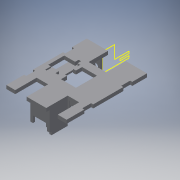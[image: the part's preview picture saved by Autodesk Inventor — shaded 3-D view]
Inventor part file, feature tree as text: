
AUTODESK INVENTOR PART (.ipt)
format: ipt  version: 2016 (Build 200138000, 138)  size: 613,376 bytes
history: native  units: in
note: dims shown in document units (in); Inventor stores cm internally (conversion verified against a paired STEP export)
features: reference x41, extrude x30, sketch x30, plane x6, projected_geometry x3
ambient origin geometry x8: Origin, YZ Plane, XZ Plane, XY Plane, X Axis, Y Axis, Z Axis, Center Point
bodies: Solid1 (feature_tree)
feature tree (110):
  extrude  "Extrusion1"  Depth=3.0in
  extrude  "Extrusion2"  Depth=0.0787in
  extrude  "Extrusion3"  Depth=1.0827in
  extrude  "Extrusion5"  Depth=1.0in TaperAngle=0.0deg
  plane  "Work Plane1"
  extrude  "Extrusion6"  Depth=0.0098in
  extrude  "Extrusion9"  Depth=0.0787in
  extrude  "Extrusion14"  Depth=0.1575in
  extrude  "Extrusion15"  Depth=1.25in
  plane  "Work Plane2"
  extrude  "Extrusion16"  Depth=0.1575in
  extrude  "Extrusion17"  Depth=0.9201in TaperAngle=0.0deg
  extrude  "Extrusion18"  Depth=0.1969in
  plane  "Work Plane3"
  extrude  "Extrusion20"  Depth=0.1969in TaperAngle=0.0deg
  extrude  "Extrusion21"  Depth=0.1181in TaperAngle=0.0deg
  plane  "Work Plane4"
  plane  "Work Plane5"
  extrude  "Extrusion23"  Depth=0.1181in
  extrude  "Extrusion24"  Depth=0.1969in TaperAngle=0.0deg
  plane  "Work Plane6"
  extrude  "Extrusion25"  Depth=0.35in
  extrude  "Extrusion26"  Depth=0.2in
  extrude  "Extrusion27"  Depth=0.1969in TaperAngle=0.0deg
  extrude  "Extrusion28"  Depth=1.5in
  extrude  "Extrusion29"  Depth=0.1181in
  extrude  "Extrusion30"  Depth=0.1181in TaperAngle=0.0deg
  extrude  "Extrusion31"  Depth=1.0in
  extrude  "Extrusion34"  Depth=0.5in
  sketch  "Sketch36"  dims[d105=0.1181in d106=0.5in]
  extrude  "Extrusion35"  Depth=0.5in
  extrude  "Extrusion36"  Depth=0.0197in
  extrude  "Extrusion37"  Depth=0.325in
  extrude  "Extrusion38"  Depth=0.1969in
  extrude  "Extrusion39"  Depth=0.1181in
  sketch  "Sketch41"  dims[d117=0.1969in d118=0.1181in]
  extrude  "Extrusion40"  Depth=0.1575in TaperAngle=0.0deg
  extrude  "Extrusion41"  Depth=1.0in TaperAngle=0.0deg
  sketch  "Sketch1"  dims[d0=4.5in d1=3.0in]
  sketch  "Sketch2"  dims[d2=0.1969in d3=0.0in d5=0.0787in]
  reference  "Reference1"
  reference  "Reference2"
  sketch  "Sketch3"  dims[d6=1.0in d7=0.0in d8=1.0827in]
  sketch  "Sketch5"  dims[d9=0.3937in d10=1.0in d11=0.0in]
  reference  "Reference14"
  reference  "Reference15"
  reference  "Reference16"
  reference  "Reference17"
  reference  "Reference18"
  sketch  "Sketch6"  dims[d12=0.0787in d23=0.0098in]
  reference  "Reference19"
  sketch  "Sketch9"  dims[d24=0.1575in d25=0.0787in]
  projected_geometry  "Projected Loop2"
  sketch  "Sketch14"  dims[d26=0.0098in d27=0.1575in]
  sketch  "Sketch15"  dims[d28=0.1181in d29=0.0in d30=1.25in]
  sketch  "Sketch16"  dims[d31=0.1575in d32=0.1575in]
  reference  "Reference30"
  sketch  "Sketch17"  dims[d33=0.1181in d34=0.0in d46=0.9201in d47=0.0in]
  reference  "Reference31"
  reference  "Reference32"
  reference  "Reference33"
  reference  "Reference35"
  reference  "Reference36"
  reference  "Reference37"
  reference  "Reference38"
  reference  "Reference39"
  reference  "Reference40"
  reference  "Reference41"
  reference  "Reference42"
  reference  "Reference43"
  reference  "Reference44"
  reference  "Reference45"
  reference  "Reference46"
  reference  "Reference47"
  reference  "Reference48"
  reference  "Reference49"
  sketch  "Sketch20"  dims[d58=0.1969in d59=0.1969in]
  reference  "Reference50"
  sketch  "Sketch21"  dims[d60=0.1969in d61=0.1969in d62=0.0in]
  sketch  "Sketch23"  dims[d63=1.0in d64=0.0in d65=0.1181in d66=0.0in]
  reference  "Reference53"
  reference  "Reference54"
  sketch  "Sketch24"  dims[d67=0.1969in d68=0.0in d69=0.1181in]
  sketch  "Sketch25"  dims[d70=0.1181in d71=0.1969in d72=0.0in]
  reference  "Reference55"
  reference  "Reference56"
  sketch  "Sketch26"  dims[d75=0.0394in d76=0.35in]
  reference  "Reference57"
  reference  "Reference58"
  sketch  "Sketch28"  dims[d77=0.1628in d78=0.2in]
  sketch  "Sketch29"  dims[d79=0.0787in d80=0.0in d81=0.1969in d82=0.0in]
  sketch  "Sketch30"  dims[d89=1.5in d90=1.5in]
  reference  "Reference59"
  sketch  "Sketch31"  dims[d91=0.1181in d92=0.0in d93=0.7in]
  sketch  "Sketch32"  dims[d94=1.26in d95=0.0in d96=0.1181in d97=0.0in]
  sketch  "Sketch35"  dims[d98=0.1181in d99=0.0in d104=1.0in]
  reference  "Reference61"
  sketch  "Sketch37"  dims[d107=1.0in d108=0.5in]
  reference  "Reference62"
  sketch  "Sketch38"  dims[d109=10.0in d110=0.0in d111=0.0197in]
  reference  "Reference63"
  sketch  "Sketch39"  dims[d112=0.0197in d113=0.325in]
  reference  "Reference64"
  sketch  "Sketch40"  dims[d114=0.197in d115=0.0in d116=0.1969in]
  reference  "Reference65"
  projected_geometry  "Projected Loop6"
  sketch  "Sketch42"  dims[d119=0.1969in d120=0.0in d121=0.1575in d122=0.0in]
  projected_geometry  "Projected Loop7"
  sketch  "Sketch43"  dims[d123=0.1in d124=0.0in d132=1.0in d133=0.0in d134=0.5in d135=0.5in d136=0.0039in d137=0.0039in d138=0.0984in d139=0.0984in d140=0.0039in d141=0.0984in d142=1.61in d143=0.0in d144=0.2in d145=0.0in d146=0.1181in d147=0.85in d148=0.0in d149=1.2in d150=0.1181in d151=1.1in d152=0.0in d153=0.28in d154=3.0in d155=0.0in d156=989.0in d157=0.0in d158=0.0098in d159=0.0098in d160=0.0098in d161=1.0in d162=0.0in]
  reference  "Reference66"
